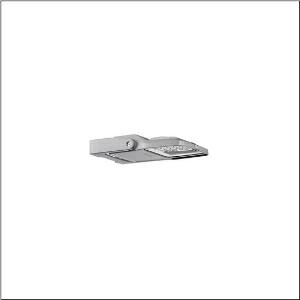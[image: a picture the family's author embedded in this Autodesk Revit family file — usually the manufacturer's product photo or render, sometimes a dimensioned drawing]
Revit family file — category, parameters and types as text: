
# Revit family: floodlight_fl_21_iq_micro___pl64_5xa7761a4e2a_05f9
name_source: partatom
category: Lighting Fixtures
units: mm (PartAtom-declared; Revit-internal decimal feet)

## family parameters
Cut with Voids When Loaded = No
Host = Face
Light Source = No
Part Type = Normal
Room Calculation Point = No
Round Connector Dimension = Use Diameter
Shared = No

## types (1)
- --- (1 x LED, 2980 lm, 23.1 W, 4000K)
    Apparent Load = 23 VA
    CIE Flux Codes = 28 80 98 100 100
    Color Rendering = 70
    Color Temperature = 4000K
    Default Elevation = 1800 mm
    Description = Floodlight FL 21 iQ micro, floodlight, primary light control with lens, of PMMA, primary optical cover: protective disc, of toughened safety glass, transparent, light distribution: PL64, light emission: direct distribution, installation type: surface-mounted, lamps: LED, High Power LED, rated values: 2.980lm | 23,1W | 129lm/W (begin service life); end service life: 2.980lm | 23,8W; at 50% lumin. flux: 1.490lm | 11W | 135,5lm/W, colour temperature: 4000K, colour rendering: CRI > 70, light colour: 740, light setting 1 begin service life: 100% | 2.980lm | 23,1W | 129lm/W | 4.000K, light setting 1 end service life: 23,8W, further light settings possible, control: optimised constant luminous flux control (CLO 2.0), Desk-Remote (wireless, voltage-free reading and setting of iQ features in the workshop via application-optimized NFC function/RFID function), Light-Fading, Smart-Wire, Night-Set, Lumen-Switch, Temp-Guard, Auto-Match, pre-setting: linear dimming characteristic, with terminal, 6-pole, mains connection: 220..240V, AC, 50/60Hz, luminaire housing, of diecast aluminium, powder-coated, SITECO metallic grey (DB 702S), corrosivity category C5 mid according to DIN EN ISO 12944suitable for swimming poolschlorine-resistant, sealing non-destructively replaceable, design bracket, of diecast aluminium, powder-coated, SITECO metallic grey (DB 702S), protection rating (complete): IP66, insulation class (complete): insulation class II (safety insulation), certification: CE, ENEC, VDE, protection symbol: D, impact resistance: IK07, permissible operating ambient temperature: -40..+40°C, permissible operating ambient temperature for outdoor applications: -40..+50°C, standard: DIN EN 12944, LABS conformity tested according to VDMA 24364:2018-05, packaging unit: 1 piece

Light Distribution: PL64
    Height = 65 mm
    Lamp = 1 x LED
    Lamp Light Flux = 2980 lm
    Lamp Power = 23.1 W
    Lamp count = 1
    Length = 312 mm
    Luminous efficacy = 129 lm/W
    Manufacturer = Siteco
    ModVariant = No
    Model = 5XA7761A4E2A
    Mounting Place = Wall
    Mounting Type = Surface mounted
    Number of Poles = 1
    OnlyDefault = Yes
    Power Factor = 1
    Product Name = Floodlight FL 21 iQ micro | PL64
    Product group = floodlight | wall mounted
    ProductGroupID = 2002
    Protection Class = Protection class II
    Protection Degree = IP 66
    RLX_Detail_Level = 1
    RLX_Emergency_Light_Flux = 0 lm
    RLX_Emergency_Type = 0
    RLX_Emergency_Type_DB = No
    RlxData = <blob elided: 97601 chars, md5=e7cebc89>
    Socket = socket
    Standby Power = 0 W
    System Light Flux = 2980 lm
    System Power = 23 W
    Type Comments = factory setting: luminous flux: 100 % | dim-lin: 254 | 455 mA
    Type Image = l_1006878.jpg
    URL = http://relux.com
    VarID = @adj_181081
    Voltage = 0 V
    Weight = 0.00 kg
    Width = 230 mm

## geometry (parser evidence)
native form markers: Blend x4, Sweep x13
no freeform markers — native parametric forms only
